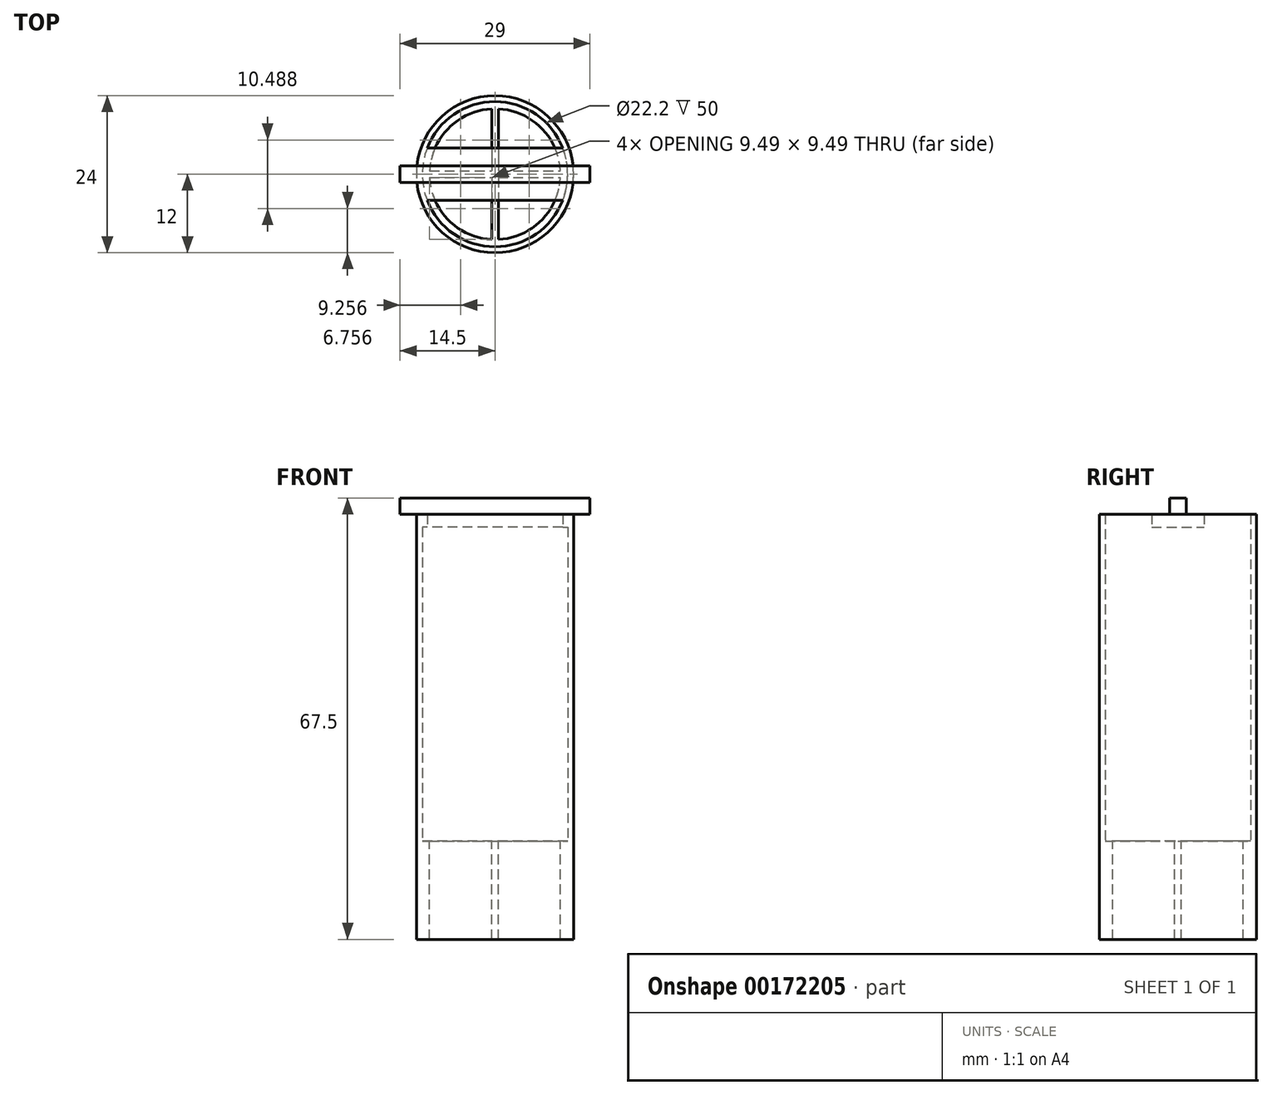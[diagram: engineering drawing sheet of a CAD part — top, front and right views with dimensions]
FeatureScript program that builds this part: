
annotation { "Feature Type Name" : "Feature", "Feature Type Description" : "" }
export const myFeature = defineFeature(function(context is Context, id is Id, definition is map)
    precondition{}
    {
        {
            var Q0;
            Q0=qCreatedBy(makeId("Top.planeOp"),FACE);
            var sketch = newSketch(context, id + "F0", { "sketchPlane" : qUnion([Q0])});
            skCircle(sketch, "E0", {"center": v(0, 0) * mm, "radius": 12 * mm});
            skSolve(sketch);
        }
        {
            var Q0;
            Q0=qSketchRegion(id+"F0",true);
            extrude(context, id + "F1", {"entities" : qUnion([Q0]), "depth" : 15 * mm});
        }
        {
            var Q0;
            Q0=makeQuery(id+"F1.opExtrude","CAP_FACE",FACE,{"disambiguationData":[OSD([sQuery(id+"F0.wireOp",EDGE,"E0")])],"isStart":false});
            var sketch = newSketch(context, id + "F2", { "sketchPlane" : qUnion([Q0])});
            skCircle(sketch, "E1", {"center": v(0, 0) * mm, "radius": 10 * mm});
            skLineSegment(sketch, "E2.bottom", {"start": v(0.5, 9.99) * mm, "end": v(-0.5, 9.99) * mm});
            skLineSegment(sketch, "E2.top", {"start": v(0.5, -9.99) * mm, "end": v(-0.5, -9.99) * mm});
            skLineSegment(sketch, "E2.left", {"start": v(0.5, 9.99) * mm, "end": v(0.5, -9.99) * mm});
            skLineSegment(sketch, "E2.right", {"start": v(-0.5, 9.99) * mm, "end": v(-0.5, -9.99) * mm});
            skLineSegment(sketch, "E3.bottom", {"start": v(-9.99, 0.5) * mm, "end": v(9.99, 0.5) * mm});
            skLineSegment(sketch, "E3.top", {"start": v(-9.99, -0.5) * mm, "end": v(9.99, -0.5) * mm});
            skLineSegment(sketch, "E3.left", {"start": v(-9.99, 0.5) * mm, "end": v(-9.99, -0.5) * mm});
            skLineSegment(sketch, "E3.right", {"start": v(9.99, 0.5) * mm, "end": v(9.99, -0.5) * mm});
            skSolve(sketch);
        }
        {
            var Q0;
            {var subQ0=sQuery(id+"F2.wireOp",EDGE,"E2.right");var subQ3=sQuery(id+"F2.wireOp",EDGE,"E3.bottom");var subQ5=makeQuery(id+"F2.imprint","INTERSECT",VERTEX,{"derivedFrom":[subQ0,subQ3]});Q0=makeQuery(id+"F2.imprint","IMPRINT",FACE,{"disambiguationData":[TD([[makeQuery(id+"F2.imprint","IMPRINT",EDGE,{"disambiguationData":[TD([[subQ5,1.0]])],"derivedFrom":subQ0}),-1.0]])]});}
            var Q1;
            {var subQ0=sQuery(id+"F2.wireOp",EDGE,"E2.left");var subQ3=sQuery(id+"F2.wireOp",EDGE,"E3.bottom");var subQ5=makeQuery(id+"F2.imprint","INTERSECT",VERTEX,{"derivedFrom":[subQ0,subQ3]});Q1=makeQuery(id+"F2.imprint","IMPRINT",FACE,{"disambiguationData":[TD([[makeQuery(id+"F2.imprint","IMPRINT",EDGE,{"disambiguationData":[TD([[subQ5,1.0]])],"derivedFrom":subQ0}),1.0]])]});}
            var Q2;
            {var subQ0=sQuery(id+"F2.wireOp",EDGE,"E2.left");var subQ3=sQuery(id+"F2.wireOp",EDGE,"E3.top");var subQ5=makeQuery(id+"F2.imprint","INTERSECT",VERTEX,{"derivedFrom":[subQ0,subQ3]});Q2=makeQuery(id+"F2.imprint","IMPRINT",FACE,{"disambiguationData":[TD([[makeQuery(id+"F2.imprint","IMPRINT",EDGE,{"disambiguationData":[TD([[subQ5,-1.0]])],"derivedFrom":subQ0}),1.0]])]});}
            var Q3;
            {var subQ0=sQuery(id+"F2.wireOp",EDGE,"E2.right");var subQ3=sQuery(id+"F2.wireOp",EDGE,"E3.top");var subQ5=makeQuery(id+"F2.imprint","INTERSECT",VERTEX,{"derivedFrom":[subQ0,subQ3]});Q3=makeQuery(id+"F2.imprint","IMPRINT",FACE,{"disambiguationData":[TD([[makeQuery(id+"F2.imprint","IMPRINT",EDGE,{"disambiguationData":[TD([[subQ5,-1.0]])],"derivedFrom":subQ0}),-1.0]])]});}
            extrude(context, id + "F3", {"entities" : qUnion([Q0, Q1, Q2, Q3]), "operationType" : NewBodyOperationType.REMOVE, "endBound" : BoundingType.THROUGH_ALL, "oppositeDirection" : true, "depth" : 13 * mm});
        }
        {
            var Q0;
            Q0=makeQuery(id+"F1.opExtrude","CAP_FACE",FACE,{"disambiguationData":[OSD([sQuery(id+"F0.wireOp",EDGE,"E0")])],"isStart":false});
            var sketch = newSketch(context, id + "F4", { "sketchPlane" : qUnion([Q0])});
            skCircle(sketch, "E4", {"center": v(0, 0) * mm, "radius": 12 * mm});
            skCircle(sketch, "E5", {"center": v(0, 0) * mm, "radius": 11.1 * mm});
            skSolve(sketch);
        }
        {
            var Q0;
            Q0=qSketchRegion(id+"F4",true);
            extrude(context, id + "F5", {"entities" : qUnion([Q0]), "operationType" : NewBodyOperationType.ADD, "depth" : 50 * mm});
        }
        {
            var Q0;
            Q0=makeQuery(id+"F5.opExtrude","CAP_FACE",FACE,{"disambiguationData":[OSD([sQuery(id+"F4.wireOp",EDGE,"E4"),sQuery(id+"F4.wireOp",EDGE,"E5")])],"isStart":false});
            var sketch = newSketch(context, id + "F6", { "sketchPlane" : qUnion([Q0])});
            skLineSegment(sketch, "E6.bottom", {"start": v(14.81, -4) * mm, "end": v(-14.81, -4) * mm});
            skLineSegment(sketch, "E6.top", {"start": v(14.81, 4) * mm, "end": v(-14.81, 4) * mm});
            skLineSegment(sketch, "E6.left", {"start": v(14.81, -4) * mm, "end": v(14.81, 4) * mm});
            skLineSegment(sketch, "E6.right", {"start": v(-14.81, -4) * mm, "end": v(-14.81, 4) * mm});
            skPoint(sketch, "E6.middle", {"position": v(0, 0) * mm});
            skLineSegment(sketch, "E7.bottom", {"start": v(-14.81, 4) * mm, "end": v(15.46, 4) * mm});
            skLineSegment(sketch, "E7.top", {"start": v(-14.81, 13.03) * mm, "end": v(15.46, 13.03) * mm});
            skLineSegment(sketch, "E7.left", {"start": v(-14.81, 4) * mm, "end": v(-14.81, 13.03) * mm});
            skLineSegment(sketch, "E7.right", {"start": v(15.46, 4) * mm, "end": v(15.46, 13.03) * mm});
            skLineSegment(sketch, "E8.bottom", {"start": v(-14.81, -4) * mm, "end": v(14.97, -4) * mm});
            skLineSegment(sketch, "E8.top", {"start": v(-14.81, -14.85) * mm, "end": v(14.97, -14.85) * mm});
            skLineSegment(sketch, "E8.left", {"start": v(-14.81, -4) * mm, "end": v(-14.81, -14.85) * mm});
            skLineSegment(sketch, "E8.right", {"start": v(14.97, -4) * mm, "end": v(14.97, -14.85) * mm});
            skSolve(sketch);
        }
        {
            var Q0;
            {var subQ0=sQuery(id+"F6.wireOp",EDGE,"E7.bottom");var subQ1=makeQuery(id+"F5.opExtrude","CAP_EDGE",EDGE,{"disambiguationData":[OSD([sQuery(id+"F4.wireOp",EDGE,"E5")])],"isStart":false});var subQ2=makeQuery(id+"F6.imprint","INTERSECT",VERTEX,{"disambiguationData":[OD(0.0)],"derivedFrom":[subQ1,subQ0]});Q0=makeQuery(id+"F6.imprint","IMPRINT",FACE,{"disambiguationData":[TD([[makeQuery(id+"F6.imprint","IMPRINT",EDGE,{"disambiguationData":[TD([[subQ2,-1.0]])],"derivedFrom":subQ0}),1.0]])]});}
            var Q1;
            {var subQ0=sQuery(id+"F6.wireOp",EDGE,"E8.bottom");var subQ1=makeQuery(id+"F5.opExtrude","CAP_EDGE",EDGE,{"disambiguationData":[OSD([sQuery(id+"F4.wireOp",EDGE,"E5")])],"isStart":false});var subQ2=makeQuery(id+"F6.imprint","INTERSECT",VERTEX,{"disambiguationData":[OD(0.0)],"derivedFrom":[subQ1,subQ0]});Q1=makeQuery(id+"F6.imprint","IMPRINT",FACE,{"disambiguationData":[TD([[makeQuery(id+"F6.imprint","IMPRINT",EDGE,{"disambiguationData":[TD([[subQ2,-1.0]])],"derivedFrom":subQ0}),-1.0]])]});}
            var Q2;
            Q2=makeQuery(id+"F6.imprint","IMPRINT",FACE,{"disambiguationData":[TD([[makeQuery(id+"F6.imprint","IMPRINT",EDGE,{"derivedFrom":sQuery(id+"F6.wireOp",EDGE,"E7.top")}),-1.0]])]});
            var Q3;
            Q3=makeQuery(id+"F6.imprint","IMPRINT",FACE,{"disambiguationData":[TD([[makeQuery(id+"F6.imprint","IMPRINT",EDGE,{"derivedFrom":sQuery(id+"F6.wireOp",EDGE,"E8.top")}),1.0]])]});
            var Q4;
            {var subQ0=sQuery(id+"F6.wireOp",EDGE,"E7.bottom");var subQ1=makeQuery(id+"F5.opExtrude","CAP_EDGE",EDGE,{"disambiguationData":[OSD([sQuery(id+"F4.wireOp",EDGE,"E4")])],"isStart":false});var subQ2=makeQuery(id+"F6.imprint","INTERSECT",VERTEX,{"disambiguationData":[OD(0.0)],"derivedFrom":[subQ1,subQ0]});Q4=makeQuery(id+"F6.imprint","IMPRINT",FACE,{"disambiguationData":[TD([[makeQuery(id+"F6.imprint","IMPRINT",EDGE,{"disambiguationData":[TD([[subQ2,-1.0]])],"derivedFrom":subQ0}),1.0]])]});}
            var Q5;
            {var subQ0=sQuery(id+"F6.wireOp",EDGE,"E8.bottom");var subQ1=makeQuery(id+"F5.opExtrude","CAP_EDGE",EDGE,{"disambiguationData":[OSD([sQuery(id+"F4.wireOp",EDGE,"E4")])],"isStart":false});var subQ2=makeQuery(id+"F6.imprint","INTERSECT",VERTEX,{"disambiguationData":[OD(0.0)],"derivedFrom":[subQ1,subQ0]});Q5=makeQuery(id+"F6.imprint","IMPRINT",FACE,{"disambiguationData":[TD([[makeQuery(id+"F6.imprint","IMPRINT",EDGE,{"disambiguationData":[TD([[subQ2,-1.0]])],"derivedFrom":subQ0}),-1.0]])]});}
            extrude(context, id + "F7", {"entities" : qUnion([Q0, Q1, Q2, Q3, Q4, Q5]), "operationType" : NewBodyOperationType.REMOVE, "oppositeDirection" : true, "depth" : 50 * mm});
        }
        {
            var Q0;
            Q0=makeQuery(id+"F7.boolean.opBoolean","SPLIT",FACE,{"disambiguationData":[OD(1.0)],"derivedFrom":makeQuery(id+"F5.opExtrude","CAP_FACE",FACE,{"disambiguationData":[OSD([sQuery(id+"F4.wireOp",EDGE,"E4"),sQuery(id+"F4.wireOp",EDGE,"E5")])],"isStart":false})});
            var sketch = newSketch(context, id + "F8", { "sketchPlane" : qUnion([Q0])});
            skLineSegment(sketch, "E9.bottom", {"start": v(11.31, 4) * mm, "end": v(-11.31, 4) * mm});
            skLineSegment(sketch, "E9.top", {"start": v(11.31, -4) * mm, "end": v(-11.31, -4) * mm});
            skLineSegment(sketch, "E9.left", {"start": v(11.31, 4) * mm, "end": v(11.31, -4) * mm});
            skLineSegment(sketch, "E9.right", {"start": v(-11.31, 4) * mm, "end": v(-11.31, -4) * mm});
            skPoint(sketch, "E9.middle", {"position": v(0, 0) * mm});
            skSolve(sketch);
        }
        {
            var Q0;
            Q0=qSketchRegion(id+"F8",true);
            extrude(context, id + "F9", {"entities" : qUnion([Q0]), "operationType" : NewBodyOperationType.ADD, "oppositeDirection" : true, "depth" : 2 * mm});
        }
        {
            var Q0;
            {var subQ0=makeQuery(id+"F5.opExtrude","CAP_FACE",FACE,{"disambiguationData":[OSD([sQuery(id+"F4.wireOp",EDGE,"E4"),sQuery(id+"F4.wireOp",EDGE,"E5")])],"isStart":false});Q0=makeQuery(id+"F9.boolean.opBoolean","MERGE",FACE,{"derivedFrom":[makeQuery(id+"F7.boolean.opBoolean","SPLIT",FACE,{"disambiguationData":[OD(0.0)],"derivedFrom":subQ0}),makeQuery(id+"F7.boolean.opBoolean","SPLIT",FACE,{"disambiguationData":[OD(1.0)],"derivedFrom":subQ0}),makeQuery(id+"F9.opExtrude","CAP_FACE",FACE,{"disambiguationData":[OSD([sQuery(id+"F8.wireOp",EDGE,"E9.bottom"),sQuery(id+"F8.wireOp",EDGE,"E9.top"),sQuery(id+"F8.wireOp",EDGE,"E9.left"),sQuery(id+"F8.wireOp",EDGE,"E9.right")])],"isStart":true})]});}
            var sketch = newSketch(context, id + "F10", { "sketchPlane" : qUnion([Q0])});
            skLineSegment(sketch, "E10.bottom", {"start": v(14.5, -1.25) * mm, "end": v(-14.5, -1.25) * mm});
            skLineSegment(sketch, "E10.top", {"start": v(14.5, 1.25) * mm, "end": v(-14.5, 1.25) * mm});
            skLineSegment(sketch, "E10.left", {"start": v(14.5, -1.25) * mm, "end": v(14.5, 1.25) * mm});
            skLineSegment(sketch, "E10.right", {"start": v(-14.5, -1.25) * mm, "end": v(-14.5, 1.25) * mm});
            skPoint(sketch, "E10.middle", {"position": v(0, 0) * mm});
            skSolve(sketch);
        }
        {
            var Q0;
            Q0=qSketchRegion(id+"F10",true);
            extrude(context, id + "F11", {"entities" : qUnion([Q0]), "operationType" : NewBodyOperationType.ADD, "depth" : 2.5 * mm});
        }
    });
